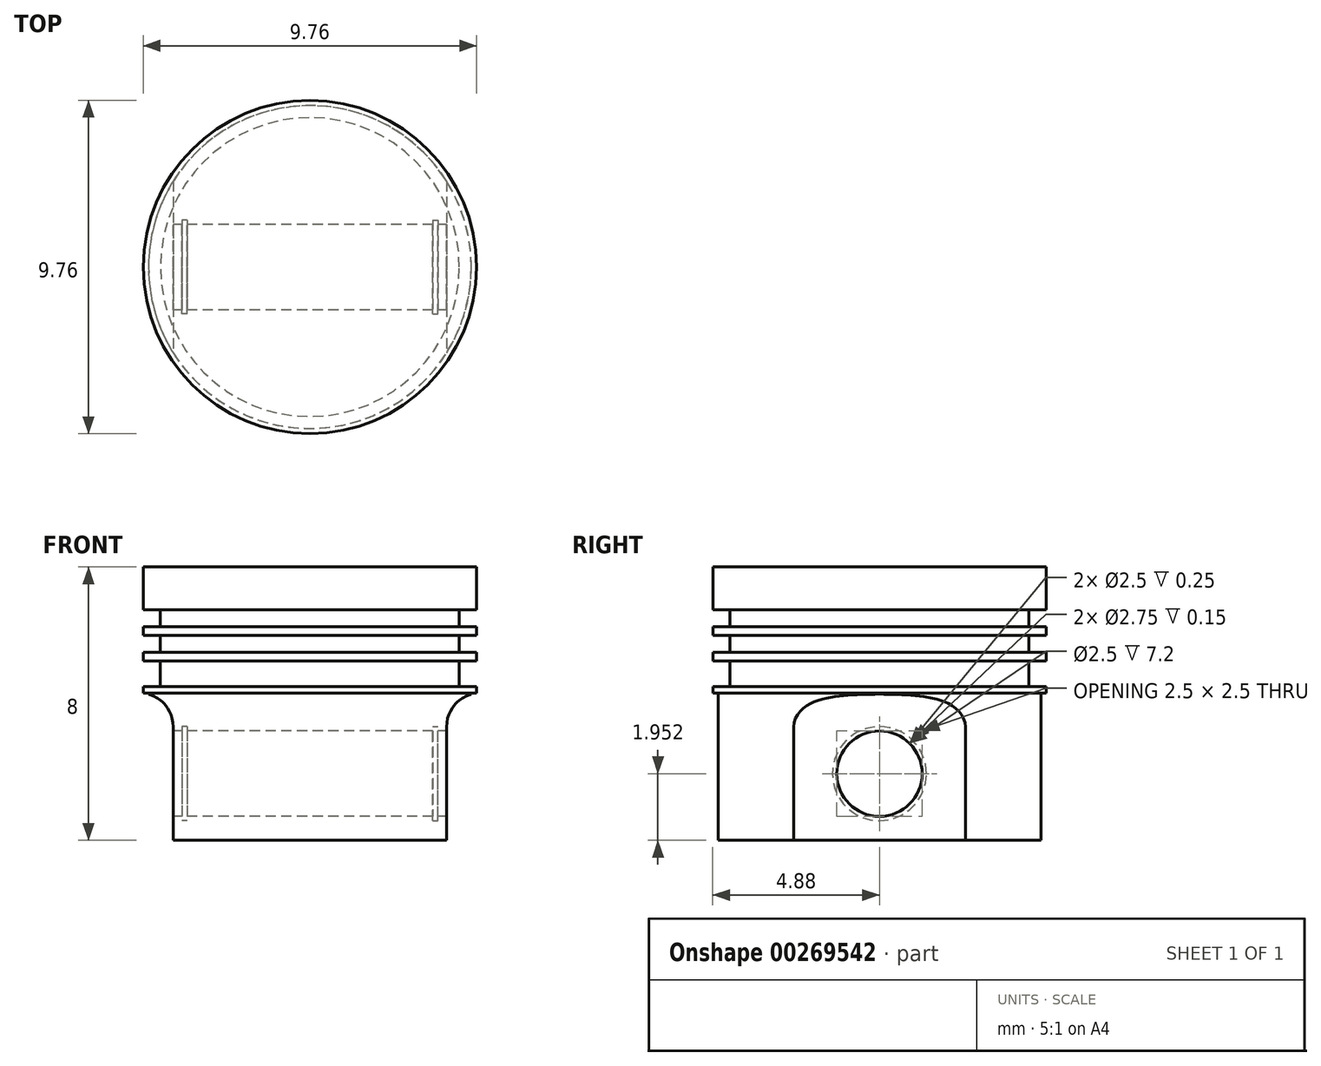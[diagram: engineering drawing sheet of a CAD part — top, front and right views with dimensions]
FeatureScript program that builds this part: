
annotation { "Feature Type Name" : "Feature", "Feature Type Description" : "" }
export const myFeature = defineFeature(function(context is Context, id is Id, definition is map)
    precondition{}
    {
        {
            var Q0;
            Q0=qCreatedBy(makeId("Top.planeOp"),FACE);
            var sketch = newSketch(context, id + "F0", { "sketchPlane" : qUnion([Q0])});
            skCircle(sketch, "E0", {"center": v(0, 0) * mm, "radius": 4.88 * mm});
            skSolve(sketch);
        }
        {
            var Q0;
            Q0 = qSketchRegion(id + "F0", true);
            extrude(context, id + "F1", {"entities" : qUnion([Q0]), "depth" : 7 * mm});
        }
        {
            var Q0;
            Q0=qCreatedBy(makeId("Front.planeOp"),FACE);
            var sketch = newSketch(context, id + "F2", { "sketchPlane" : qUnion([Q0])});
            skLineSegment(sketch, "E1", {"start": v(-4, 3.32) * mm, "end": v(-4, 0) * mm});
            skLineSegment(sketch, "E2", {"start": v(-4, 0) * mm, "end": v(-5, 0) * mm});
            skLineSegment(sketch, "E3", {"start": v(-5, 0) * mm, "end": v(-5, 4.32) * mm});
            skLineSegment(sketch, "E4", {"start": v(-5, 4.32) * mm, "end": v(-5, 4.32) * mm});
            skArc(sketch, "E5.filletArc", {"start": v(-4, 3.32) * mm, "mid": v(-4.3, 4.02) * mm, "end": v(-5, 4.32) * mm});
            skArc(sketch, "E6.MirrorCS", {"start": v(4, 3.32) * mm, "mid": v(4.3, 4.02) * mm, "end": v(5, 4.32) * mm});
            skLineSegment(sketch, "E7.MirrorCS", {"start": v(5, 0) * mm, "end": v(5, 4.32) * mm});
            skLineSegment(sketch, "E8.MirrorCS", {"start": v(4, 0) * mm, "end": v(5, 0) * mm});
            skLineSegment(sketch, "E9.MirrorCS", {"start": v(4, 3.32) * mm, "end": v(4, 0) * mm});
            skSolve(sketch);
        }
        {
            var Q0;
            Q0 = qSketchRegion(id + "F2", true);
            extrude(context, id + "F3", {"entities" : qUnion([Q0]), "operationType" : NewBodyOperationType.REMOVE, "endBound" : BoundingType.SYMMETRIC, "oppositeDirection" : true, "depth" : 10 * mm});
        }
        {
            var Q0;
            Q0=qCreatedBy(makeId("Right.planeOp"),FACE);
            var sketch = newSketch(context, id + "F4", { "sketchPlane" : qUnion([Q0])});
            skCircle(sketch, "E10", {"center": v(0, 1.95) * mm, "radius": 1.25 * mm});
            skSolve(sketch);
        }
        {
            var Q0;
            Q0 = qSketchRegion(id + "F4", true);
            extrude(context, id + "F5", {"entities" : qUnion([Q0]), "operationType" : NewBodyOperationType.REMOVE, "endBound" : BoundingType.SYMMETRIC, "depth" : 10 * mm});
        }
        {
            var Q0;
            Q0=qCreatedBy(makeId("Front.planeOp"),FACE);
            var sketch = newSketch(context, id + "F6", { "sketchPlane" : qUnion([Q0])});
            skLineSegment(sketch, "E11.bottom", {"start": v(4.38, 6.25) * mm, "end": v(5.37, 6.25) * mm});
            skLineSegment(sketch, "E11.top", {"start": v(4.38, 6.75) * mm, "end": v(5.37, 6.75) * mm});
            skLineSegment(sketch, "E11.left", {"start": v(4.38, 6.25) * mm, "end": v(4.38, 6.75) * mm});
            skLineSegment(sketch, "E11.right", {"start": v(5.37, 6.25) * mm, "end": v(5.37, 6.75) * mm});
            skPoint(sketch, "E11.middle", {"position": v(4.88, 6.5) * mm});
            skLineSegment(sketch, "E12.bottom", {"start": v(4.38, 6) * mm, "end": v(5.38, 6) * mm});
            skLineSegment(sketch, "E12.top", {"start": v(4.38, 5.5) * mm, "end": v(5.38, 5.5) * mm});
            skLineSegment(sketch, "E12.left", {"start": v(4.38, 6) * mm, "end": v(4.38, 5.5) * mm});
            skLineSegment(sketch, "E12.right", {"start": v(5.38, 6) * mm, "end": v(5.38, 5.5) * mm});
            skPoint(sketch, "E12.middle", {"position": v(4.88, 5.75) * mm});
            skLineSegment(sketch, "E13.bottom", {"start": v(4.38, 5.25) * mm, "end": v(5.38, 5.25) * mm});
            skLineSegment(sketch, "E13.top", {"start": v(4.38, 4.5) * mm, "end": v(5.38, 4.5) * mm});
            skLineSegment(sketch, "E13.left", {"start": v(4.38, 5.25) * mm, "end": v(4.38, 4.5) * mm});
            skLineSegment(sketch, "E13.right", {"start": v(5.38, 5.25) * mm, "end": v(5.38, 4.5) * mm});
            skPoint(sketch, "E13.middle", {"position": v(4.88, 4.88) * mm});
            skLineSegment(sketch, "E14", {"start": v(0, 0) * mm, "end": v(0, 7.28) * mm, "construction": true});
            skLineSegment(sketch, "E15.bottom", {"start": v(5.38, 4.3) * mm, "end": v(4.73, 4.3) * mm});
            skLineSegment(sketch, "E15.top", {"start": v(5.38, 0) * mm, "end": v(4.73, 0) * mm});
            skLineSegment(sketch, "E15.left", {"start": v(5.38, 4.3) * mm, "end": v(5.38, 0) * mm});
            skLineSegment(sketch, "E15.right", {"start": v(4.73, 4.3) * mm, "end": v(4.73, 0) * mm});
            skPoint(sketch, "E15.middle", {"position": v(5.05, 2.15) * mm});
            skSolve(sketch);
        }
        {
            var Q0;
            Q0 = qSketchRegion(id + "F6", true);
            var Q1;
            Q1=sQuery(id+"F6.wireOp",EDGE,"E14");
            revolve(context, id + "F7", {"operationType" : NewBodyOperationType.REMOVE, "entities" : qUnion([Q0]), "axis" : qUnion([Q1]), "revolveType" : RevolveType.FULL, "oppositeDirection" : true});
        }
        {
            var Q0;
            Q0=makeQuery(id+"F1.opExtrude","CAP_FACE",FACE,{"disambiguationData":[OSD([sQuery(id+"F0.wireOp",EDGE,"E0")])],"isStart":false});
            extrude(context, id + "F8", {"entities" : qUnion([Q0]), "operationType" : NewBodyOperationType.ADD, "depth" : 1 * mm});
        }
        {
            var Q0;
            Q0=makeQuery(id+"F3.boolean.opBoolean","COPY",FACE,{"derivedFrom":makeQuery(id+"F3.opExtrude","SWEPT_FACE",FACE,{"disambiguationData":[OSD([sQuery(id+"F2.wireOp",EDGE,"E9.MirrorCS")])]})});
            cPlane(context, id + "F9", {"entities" : qUnion([Q0]), "cplaneType" : CPlaneType.OFFSET, "offset" : .25 * mm, "oppositeDirection" : true, "width" : 150 * mm, "height" : 150 * mm});
        }
        {
            var Q0;
            Q0=qCreatedBy(id+"F9.planeOp",FACE);
            var sketch = newSketch(context, id + "F10", { "sketchPlane" : qUnion([Q0])});
            skCircle(sketch, "E16", {"center": v(0, 1.95) * mm, "radius": 1.38 * mm});
            skCircle(sketch, "E17", {"center": v(0, 1.95) * mm, "radius": 1.25 * mm});
            skSolve(sketch);
        }
        {
            var Q0;
            Q0 = qSketchRegion(id + "F10", true);
            extrude(context, id + "F11", {"entities" : qUnion([Q0]), "operationType" : NewBodyOperationType.REMOVE, "oppositeDirection" : true, "depth" : .15 * mm});
        }
        {
            var Q0;
            Q0=makeQuery(id+"F3.boolean.opBoolean","COPY",FACE,{"derivedFrom":makeQuery(id+"F3.opExtrude","SWEPT_FACE",FACE,{"disambiguationData":[OSD([sQuery(id+"F2.wireOp",EDGE,"E1")])]})});
            cPlane(context, id + "F12", {"entities" : qUnion([Q0]), "cplaneType" : CPlaneType.OFFSET, "offset" : .25 * mm, "oppositeDirection" : true, "width" : 150 * mm, "height" : 150 * mm});
        }
        {
            var Q0;
            Q0=qCreatedBy(id+"F12.planeOp",FACE);
            var sketch = newSketch(context, id + "F13", { "sketchPlane" : qUnion([Q0])});
            skCircle(sketch, "E18", {"center": v(0, 1.95) * mm, "radius": 1.38 * mm});
            skCircle(sketch, "E19", {"center": v(0, 1.95) * mm, "radius": 1.25 * mm});
            skSolve(sketch);
        }
        {
            var Q0;
            Q0 = qSketchRegion(id + "F13", true);
            extrude(context, id + "F14", {"entities" : qUnion([Q0]), "operationType" : NewBodyOperationType.REMOVE, "oppositeDirection" : true, "depth" : .15 * mm});
        }
    });
